# Revit family: Lighting_Emergency&Security_Linergy_Astra
name_source: partatom
category: Lighting Fixtures
revit_build: Autodesk Revit 2018 (Build: 20190510_1515(x64)
units: mm (PartAtom-declared; Revit-internal decimal feet)

## family parameters
Cut with Voids When Loaded = No
Host = Face
Light Source = Yes
OmniClass Number = 23.35.47.15
OmniClass Title = Exit Illuminated Signs
Part Type = Normal
Room Calculation Point = No
Round Connector Dimension = Use Diameter
Shared = No

## types (1)
- Default - please load Revit Family Type Catalog
    Apparent Load = 0 VA
    Apparent Load Phase 2 = 0 VA
    Apparent Load Phase 3 = 0 VA
    Arrow Opt 1 = Direction : Down
    Arrow Opt 2 = Direction : Left
    Arrow Opt 3 = Direction : Right
    BIMobject category = Emergency & Security
    Battery = Li-FePO4 3,2V 1,5Ah
    Color Filter = 16777215
    Default Elevation = 1219 mm
    Description = LED Emergency signalling luminaires.
    Design country = Italy
    Dimming Lamp Color Temperature Shift = <None>
    Duration = 1/2/3 h
    Edition number = 1
    Function = Inhibit
    IFC Classification = Light Fixture
    Input power = 2 W
    Installation instructions = https://www.linergy.it
    Insulation class = II
    Lamp type = NM/M
    Manufacturer = Linergy
    Manufacturer country = Italy
    Manufacturer name = Linergy
    Material main = PC/ABS
    Material secondary = Electronic & optical components
    Model = AS1201
    Mounting Opt 1 = Mounting : Ceiling
    Mounting Opt 2 = Mounting : Flag
    Mounting Opt 3 = Mounting : Wall
    Number of Poles = 1
    OmniClass Code = 23-35 47 15
    OmniClass Description = Exit Illuminated Signs
    Photometric Web File = generic
    Power Factor = 0
    Power supply = 230 Vac
    Product Guid = e71a8c37-d0ef-48fd-8abf-63ec5bc0de21
    Product SKU = astra
    Product certification = https://www.linergy.it
    Product data url = https://bimobject.com
    Product family = Signalling luminaires
    Product group = Signalling luminaires
    Product name = ASTRA - Emergency signalling luminaire
    Product url = https://www.linergy.it
    Protection degree = IP40
    QR code = https://bimobject.com
    Technical description = https://www.linergy.it
    Tilt Angle = 90.00°
    Type 22 = Yes
    Type 32 = No
    URL = https://www.linergy.it
    URL - Article page = https://www.linergy.it
    Viewing distance = 22 m
    Voltage = 230 V

## geometry (parser evidence)
native form markers: Sweep x14
no freeform markers — native parametric forms only
